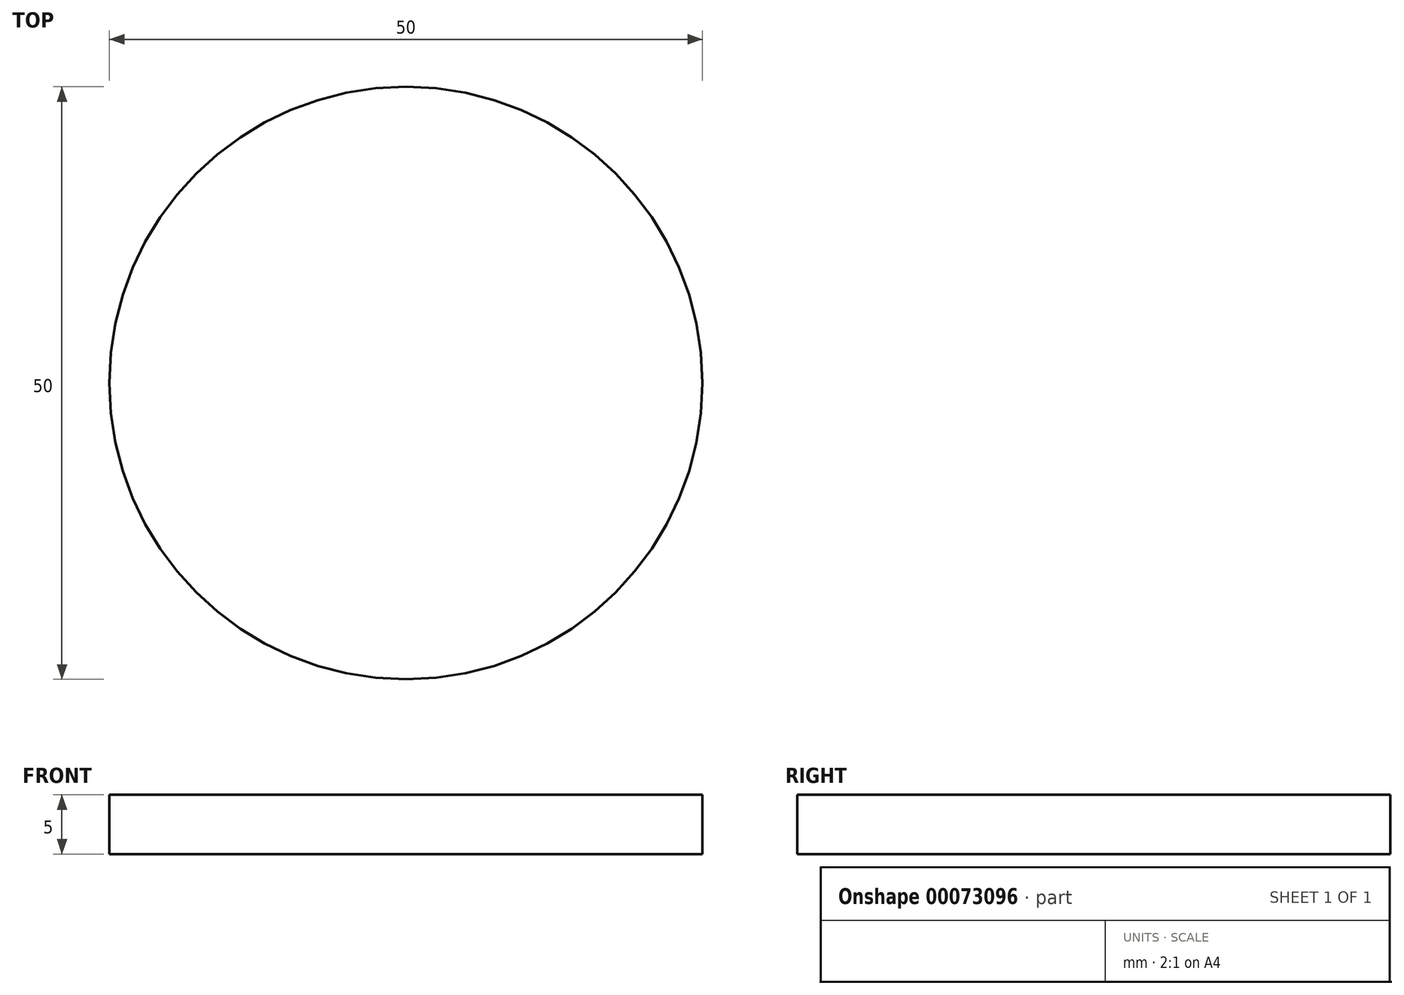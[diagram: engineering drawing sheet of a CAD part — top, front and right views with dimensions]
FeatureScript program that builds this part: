
annotation { "Feature Type Name" : "Feature", "Feature Type Description" : "" }
export const myFeature = defineFeature(function(context is Context, id is Id, definition is map)
    precondition{}
    {
        {
            var Q0;
            Q0=qCreatedBy(makeId("Top.planeOp"),FACE);
            var sketch = newSketch(context, id + "F0", { "sketchPlane" : qUnion([Q0])});
            skCircle(sketch, "E0", {"center": v(0, 0) * mm, "radius": 25 * mm});
            skSolve(sketch);
        }
        {
            var Q0;
            Q0 = qSketchRegion(id + "F0", true);
            extrude(context, id + "F1", {"entities" : qUnion([Q0]), "depth" : 5 * mm});
        }
    });
